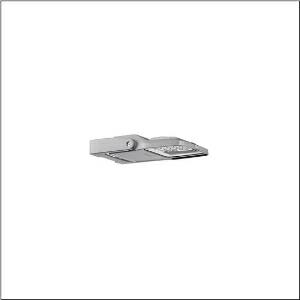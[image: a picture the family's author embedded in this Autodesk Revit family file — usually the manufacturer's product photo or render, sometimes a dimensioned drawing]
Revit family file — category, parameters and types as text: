
# Revit family: floodlight_fl_21_micro___pl33t_5xa7761a2f2a_2d9d
name_source: partatom
category: Lighting Fixtures
units: mm (PartAtom-declared; Revit-internal decimal feet)

## family parameters
Cut with Voids When Loaded = No
Host = Face
Light Source = No
Part Type = Normal
Room Calculation Point = No
Round Connector Dimension = Use Diameter
Shared = No

## types (1)
- --- (1 x LED, 2930 lm, 23.1 W, 3000K)
    Apparent Load = 23 VA
    CIE Flux Codes = 26 75 99 100 100
    Color Rendering = 70
    Color Temperature = 3000K
    Default Elevation = 1800 mm
    Description = Floodlight FL 21 micro, floodlight, primary light control with lens, of PMMA, primary optical cover: protective disc, of toughened safety glass, transparent, light distribution: PL33T, light emission: direct distribution, installation type: surface-mounted, LED, High Power LED, rated luminous flux: 2.930lm, luminous efficacy: 127lm/W, light colour: 730, colour temperature: 3000K, control gear: ECG iQ, control: optimised constant luminous flux control (CLO 2.0), Desk-Remote (wireless, voltage-free reading and setting of iQ features in the workshop via application-optimized NFC function/RFID function), Light-Fading, Smart-Wire, Night-Set, Lumen-Switch, Temp-Guard, Auto-Match, with terminal, 6-pole, mains connection: 220..240V, AC, 50/60Hz, start of lifetime: 23W, end of lifetime: 24W, reduction: 11W, luminaire housing, of diecast aluminium, powder-coated, Siteco® metallic grey (DB 702S), corrosivity category C5 according to DIN EN ISO 12944, design bracket, of diecast aluminium, powder-coated, Siteco® metallic grey (DB 702S), protection rating (complete): IP66, insulation class (complete): insulation class II (safety insulation), certification: CE, protection symbol: D, impact resistance: IK07, permissible operating ambient temperature: -40..+40°C, permissible operating ambient temperature for outdoor applications: -40..+50°C, standard: DIN EN 12944, packaging unit: 1 piece

Light Distribution: PL33T
    Height = 65 mm
    Lamp = 1 x LED
    Lamp Light Flux = 2930 lm
    Lamp Power = 23.1 W
    Lamp count = 1
    Length = 312 mm
    Luminous efficacy = 127 lm/W
    Manufacturer = Siteco
    ModVariant = No
    Model = 5XA7761A2F2A
    Number of Poles = 1
    OnlyDefault = Yes
    Power Factor = 1
    Product Name = Floodlight FL 21 micro | PL33T
    Product group = floodlight | pylon top
    ProductGroupID = 6101
    Protection Class = Protection class II
    Protection Degree = IP 66
    RLX_Detail_Level = 1
    RlxData = <blob elided: 97105 chars, md5=be4348eb>
    Socket = socket
    Standby Power = 0 W
    System Light Flux = 2930 lm
    System Power = 23 W
    Type Comments = factory setting: luminous flux: 100 % | dim-lin: 254 | 455 mA
    Type Image = l_1006878.jpg
    URL = http://relux.com
    VarID = @adj_058351
    Voltage = 0 V
    Weight = 0.00 kg
    Width = 230 mm

## geometry (parser evidence)
native form markers: Blend x4, Sweep x12
no freeform markers — native parametric forms only
